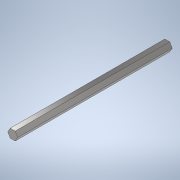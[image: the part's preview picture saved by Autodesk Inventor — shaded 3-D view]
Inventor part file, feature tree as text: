
AUTODESK INVENTOR PART (.ipt)
format: ipt  version: 2020 (Build 240168000, 168)  size: 101,376 bytes
history: native  units: in
note: dims shown in document units (in); Inventor stores cm internally (conversion verified against a paired STEP export)
features: extrude x1, sketch x1
ambient origin geometry x8: Origin, YZ Plane, XZ Plane, XY Plane, X Axis, Y Axis, Z Axis, Center Point
bodies: Solid1 (feature_tree)
feature tree (2):
  extrude  "Extrusion1"  Depth=9.0in TaperAngle=0.0deg
  sketch  "Sketch1"  dims[d0=0.5in d1=9.0in d2=0.0in]
